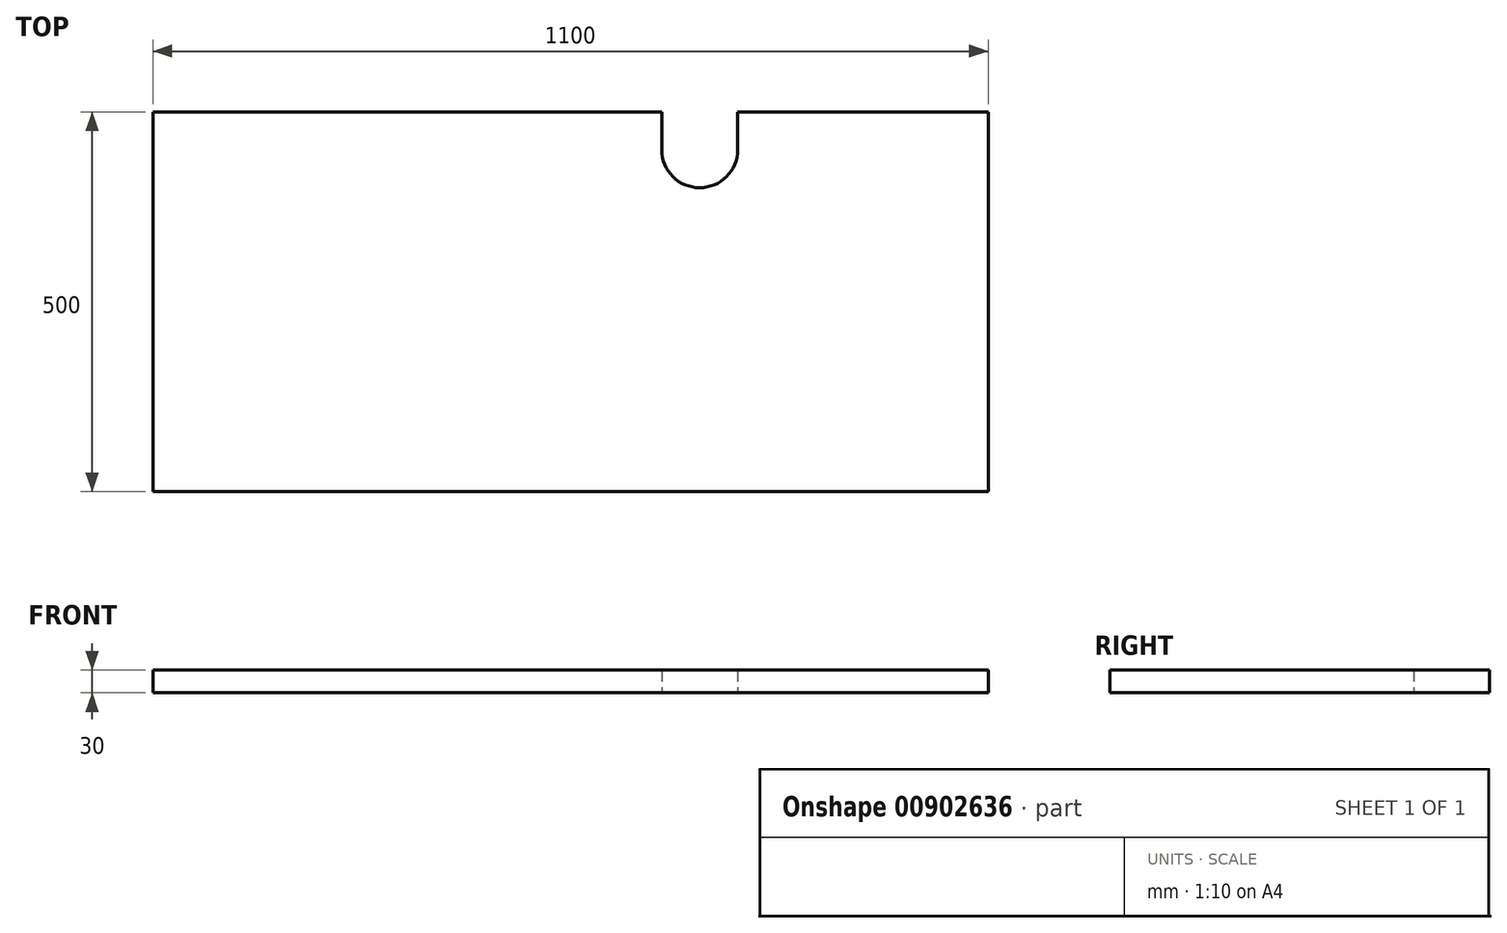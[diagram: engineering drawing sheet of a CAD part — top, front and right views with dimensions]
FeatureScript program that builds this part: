
annotation { "Feature Type Name" : "Feature", "Feature Type Description" : "" }
export const myFeature = defineFeature(function(context is Context, id is Id, definition is map)
    precondition{}
    {
        {
            var Q0;
            Q0=qCreatedBy(makeId("Top.planeOp"),FACE);
            var sketch = newSketch(context, id + "F0", { "sketchPlane" : qUnion([Q0])});
            skLineSegment(sketch, "E0.bottom", {"start": v(0, 0) * mm, "end": v(1100, 0) * mm});
            skLineSegment(sketch, "E0.top", {"start": v(0, 500) * mm, "end": v(670, 500) * mm});
            skLineSegment(sketch, "E0.left", {"start": v(0, 0) * mm, "end": v(0, 500) * mm});
            skLineSegment(sketch, "E0.right", {"start": v(1100, 0) * mm, "end": v(1100, 500) * mm});
            skArc(sketch, "E1", {"start": v(670, 450) * mm, "mid": v(720, 400) * mm, "end": v(770, 450) * mm});
            skLineSegment(sketch, "E2", {"start": v(770, 450) * mm, "end": v(770, 500) * mm});
            skLineSegment(sketch, "E3", {"start": v(670, 450) * mm, "end": v(670, 500) * mm});
            skLineSegment(sketch, "E4.trimOffspring", {"start": v(770, 500) * mm, "end": v(1100, 500) * mm});
            skSolve(sketch);
        }
        {
            var Q0;
            Q0 = qSketchRegion(id + "F0", true);
            extrude(context, id + "F1", {"entities" : qUnion([Q0]), "depth" : 30 * mm, "offsetDistance" : 25 * mm});
        }
        {
            var Q0;
            Q0=makeQuery(id+"F1.opExtrude","CAP_FACE",FACE,{"disambiguationData":[OSD([sQuery(id+"F0.wireOp",EDGE,"E0.bottom"),sQuery(id+"F0.wireOp",EDGE,"E0.top"),sQuery(id+"F0.wireOp",EDGE,"E0.left"),sQuery(id+"F0.wireOp",EDGE,"E0.right"),sQuery(id+"F0.wireOp",EDGE,"E1"),sQuery(id+"F0.wireOp",EDGE,"E2"),sQuery(id+"F0.wireOp",EDGE,"E3"),sQuery(id+"F0.wireOp",EDGE,"E4.trimOffspring")])],"isStart":true});
            var sketch = newSketch(context, id + "F2", { "sketchPlane" : qUnion([Q0])});
            skLineSegment(sketch, "E5.0", {"start": v(60, -440) * mm, "end": v(610.46, -440) * mm, "construction": true});
            skLineSegment(sketch, "E5.1", {"start": v(829.54, -440) * mm, "end": v(1040, -440) * mm, "construction": true});
            skLineSegment(sketch, "E5.2", {"start": v(1040, -440) * mm, "end": v(1040, -60) * mm, "construction": true});
            skArc(sketch, "E5.3", {"start": v(610.46, -440) * mm, "mid": v(720, -340) * mm, "end": v(829.54, -440) * mm, "construction": true});
            skLineSegment(sketch, "E5.4", {"start": v(1040, -60) * mm, "end": v(60, -60) * mm, "construction": true});
            skLineSegment(sketch, "E5.5", {"start": v(60, -60) * mm, "end": v(60, -440) * mm, "construction": true});
            skSolve(sketch);
        }
    });
